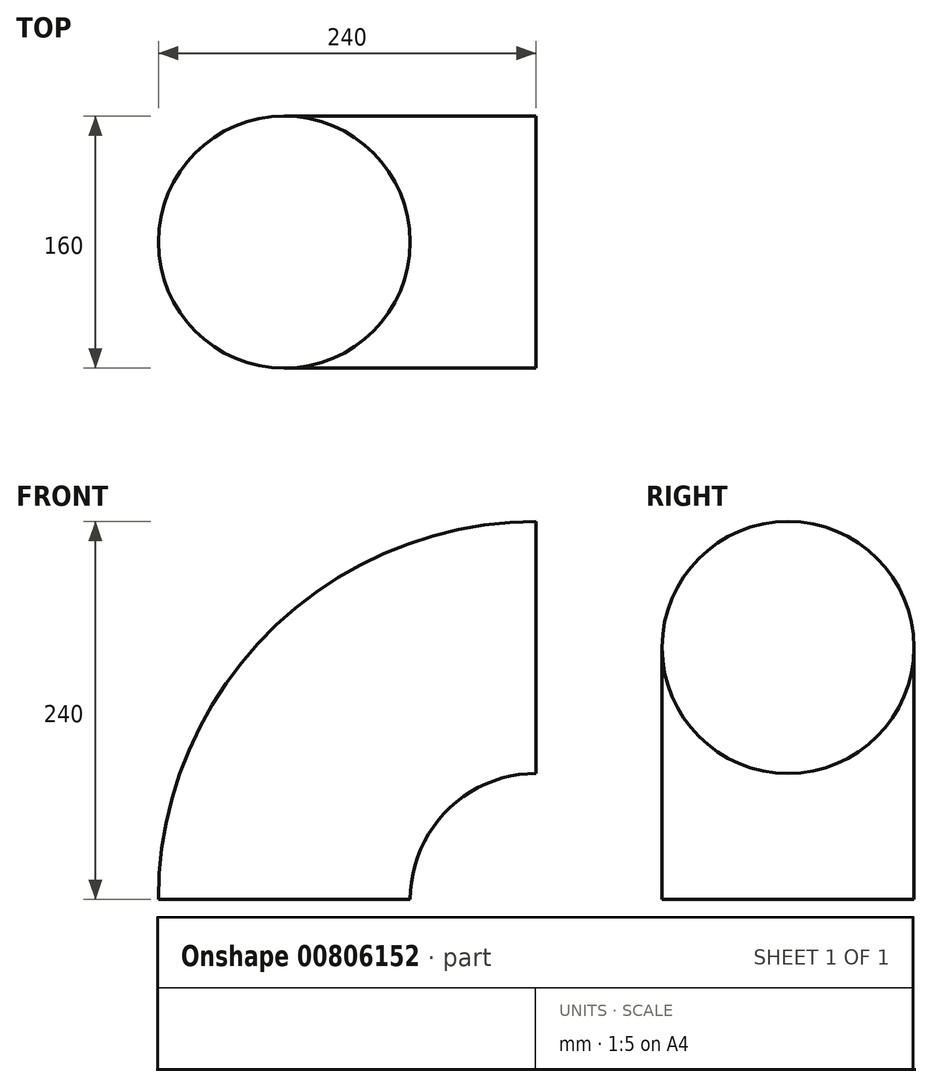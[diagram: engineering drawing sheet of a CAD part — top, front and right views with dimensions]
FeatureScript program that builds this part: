
annotation { "Feature Type Name" : "Feature", "Feature Type Description" : "" }
export const myFeature = defineFeature(function(context is Context, id is Id, definition is map)
    precondition{}
    {
        {
            var Q0;
            Q0=qCreatedBy(makeId("Front.planeOp"),FACE);
            var sketch = newSketch(context, id + "F0", { "sketchPlane" : qUnion([Q0])});
            skLineSegment(sketch, "E0", {"start": v(0, 0) * mm, "end": v(-243, 0) * mm});
            skLineSegment(sketch, "E1", {"start": v(0, 0) * mm, "end": v(0, 160) * mm});
            skArc(sketch, "E2", {"start": v(0, 160) * mm, "mid": v(-113.14, 113.14) * mm, "end": v(-160, 0) * mm});
            skSolve(sketch);
        }
        {
            var Q0;
            Q0=qCreatedBy(makeId("Right.planeOp"),FACE);
            var sketch = newSketch(context, id + "F1", { "sketchPlane" : qUnion([Q0])});
            skLineSegment(sketch, "E3", {"start": v(0, 0) * mm, "end": v(0, 160) * mm});
            skCircle(sketch, "E4", {"center": v(0, 160) * mm, "radius": 80 * mm});
            skSolve(sketch);
        }
        {
            var Q0;
            Q0=makeQuery(id+"F1.imprint","IMPRINT",FACE,{"disambiguationData":[TD([[makeQuery(id+"F1.imprint","IMPRINT",EDGE,{"derivedFrom":sQuery(id+"F1.wireOp",EDGE,"E4")}),1.0]])]});
            var Q1;
            Q1=sQuery(id+"F0.wireOp",EDGE,"E2");
            sweep(context, id + "F2", {"profiles" : qUnion([Q0]), "path" : qUnion([Q1])});
        }
    });
